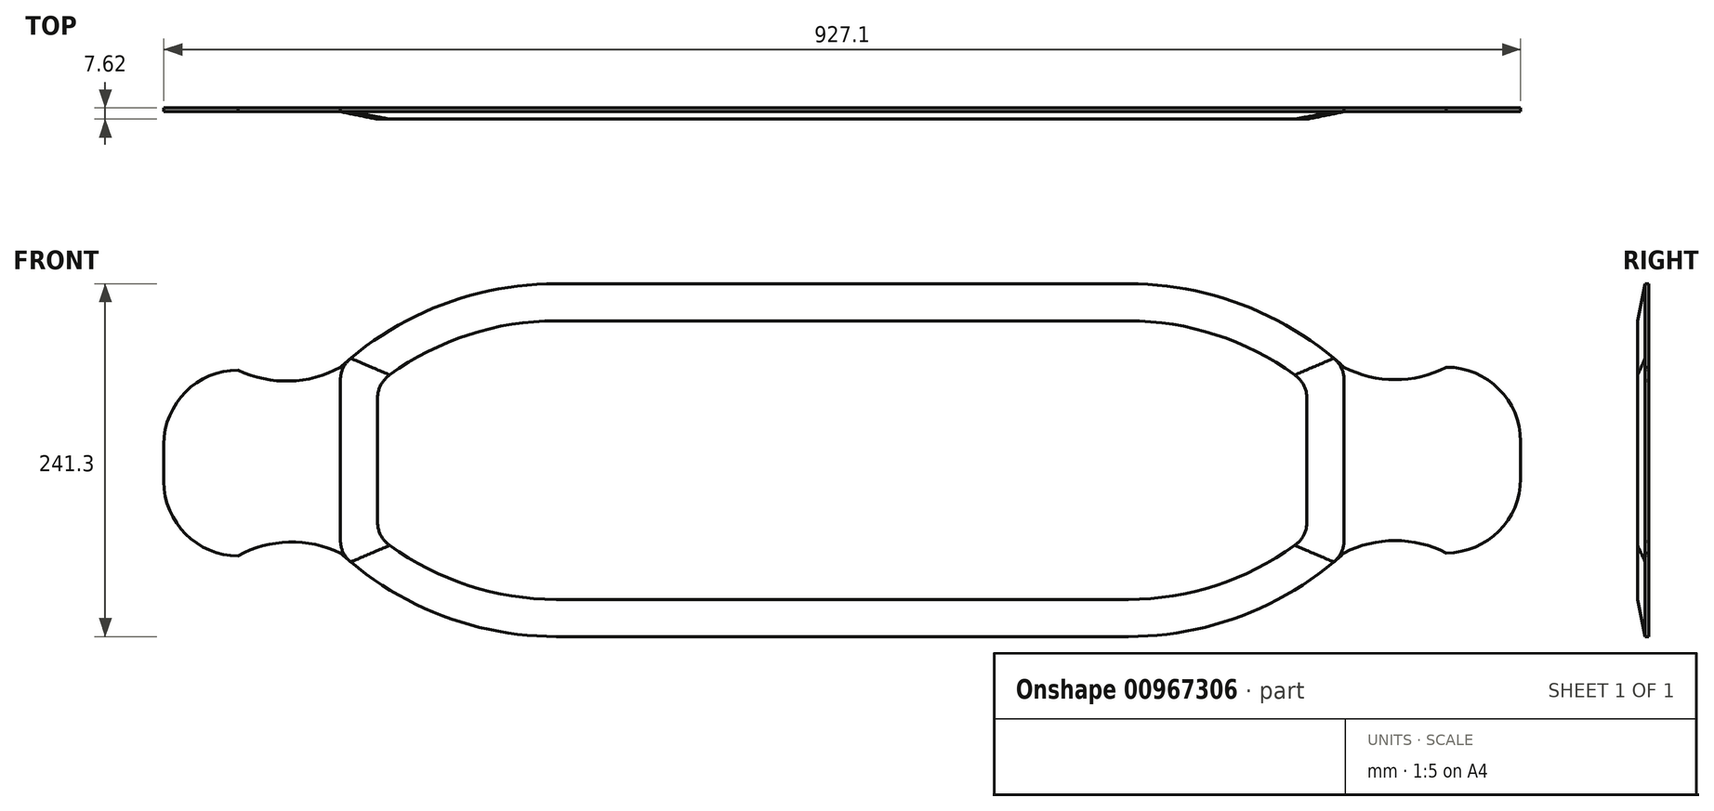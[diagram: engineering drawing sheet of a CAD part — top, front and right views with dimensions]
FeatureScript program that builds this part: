
annotation { "Feature Type Name" : "Feature", "Feature Type Description" : "" }
export const myFeature = defineFeature(function(context is Context, id is Id, definition is map)
    precondition{}
    {
        {
            var Q0;
            Q0=qCreatedBy(makeId("Front.planeOp"),FACE);
            cPlane(context, id + "F0", {"entities" : qUnion([Q0]), "cplaneType" : CPlaneType.OFFSET, "offset" : 6.35 * mm, "width" : 152.4 * mm, "height" : 152.4 * mm});
        }
        {
            var Q0;
            Q0=qCreatedBy(id+"F0.planeOp",FACE);
            var sketch = newSketch(context, id + "F1", { "sketchPlane" : qUnion([Q0])});
            skLineSegment(sketch, "E0.bottom", {"start": v(342.9, -120.65) * mm, "end": v(-342.9, -120.65) * mm});
            skLineSegment(sketch, "E0.top", {"start": v(342.9, 120.65) * mm, "end": v(-342.9, 120.65) * mm});
            skLineSegment(sketch, "E0.left", {"start": v(342.9, -120.65) * mm, "end": v(342.9, 120.65) * mm});
            skLineSegment(sketch, "E0.right", {"start": v(-342.9, -120.65) * mm, "end": v(-342.9, 120.65) * mm});
            skSolve(sketch);
        }
        {
            var Q0;
            Q0=makeQuery(id+"F1.imprint","IMPRINT",FACE,{"disambiguationData":[TD([[makeQuery(id+"F1.imprint","IMPRINT",EDGE,{"derivedFrom":sQuery(id+"F1.wireOp",EDGE,"E0.bottom")}),-1.0]])]});
            var sketch = newSketch(context, id + "F2", { "sketchPlane" : qUnion([Q0])});
            skLineSegment(sketch, "E1.left", {"start": v(-463.55, 10.74) * mm, "end": v(-463.55, -14.66) * mm});
            skPoint(sketch, "E1.middle", {"position": v(-403.23, 0) * mm});
            skLineSegment(sketch, "E2.left", {"start": v(463.55, -12.7) * mm, "end": v(463.55, 12.7) * mm});
            skPoint(sketch, "E2.middle", {"position": v(403.23, 0) * mm});
            skPoint(sketch, "E3.visualSharp", {"position": v(-463.55, 63.5) * mm});
            skArc(sketch, "E3.filletArc", {"start": v(-412.77, 61.54) * mm, "mid": v(-448.68, 46.66) * mm, "end": v(-463.55, 10.74) * mm});
            skPoint(sketch, "E4.visualSharp", {"position": v(-463.55, -63.5) * mm});
            skArc(sketch, "E4.filletArc", {"start": v(-463.55, -14.66) * mm, "mid": v(-448.68, -50.57) * mm, "end": v(-412.77, -65.46) * mm});
            skPoint(sketch, "E5.visualSharp", {"position": v(463.55, -63.5) * mm});
            skArc(sketch, "E5.filletArc", {"start": v(412.75, -63.5) * mm, "mid": v(448.67, -48.62) * mm, "end": v(463.55, -12.7) * mm});
            skPoint(sketch, "E6.visualSharp", {"position": v(463.55, 63.5) * mm});
            skArc(sketch, "E6.filletArc", {"start": v(463.55, 12.7) * mm, "mid": v(448.67, 48.62) * mm, "end": v(412.75, 63.5) * mm});
            skArc(sketch, "E7", {"start": v(-412.77, 61.54) * mm, "mid": v(-377.6, 54.04) * mm, "end": v(-342.9, 63.5) * mm});
            skArc(sketch, "E8", {"start": v(-342.9, -63.5) * mm, "mid": v(-378.07, -56) * mm, "end": v(-412.77, -65.46) * mm});
            skArc(sketch, "E9", {"start": v(342.9, 63.5) * mm, "mid": v(377.83, 55.03) * mm, "end": v(412.75, 63.5) * mm});
            skArc(sketch, "E10", {"start": v(412.75, -63.5) * mm, "mid": v(377.82, -55.03) * mm, "end": v(342.9, -63.5) * mm});
            skArc(sketch, "E11", {"start": v(-195.49, 120.65) * mm, "mid": v(-274.54, 105.86) * mm, "end": v(-342.9, 63.5) * mm});
            skArc(sketch, "E12", {"start": v(-342.9, -63.5) * mm, "mid": v(-274.54, -105.86) * mm, "end": v(-195.49, -120.65) * mm});
            skArc(sketch, "E13", {"start": v(195.49, -120.65) * mm, "mid": v(274.54, -105.86) * mm, "end": v(342.9, -63.5) * mm});
            skArc(sketch, "E14", {"start": v(342.9, 63.5) * mm, "mid": v(274.54, 105.86) * mm, "end": v(195.49, 120.65) * mm});
            skLineSegment(sketch, "E15", {"start": v(-195.49, -120.65) * mm, "end": v(195.49, -120.65) * mm});
            skLineSegment(sketch, "E16", {"start": v(195.49, 120.65) * mm, "end": v(-195.49, 120.65) * mm});
            skLineSegment(sketch, "E17", {"start": v(342.9, -63.5) * mm, "end": v(342.9, 63.5) * mm});
            skLineSegment(sketch, "E18", {"start": v(-342.9, -63.5) * mm, "end": v(-342.9, 63.5) * mm});
            skSolve(sketch);
        }
        {
            var Q0;
            Q0=makeQuery(id+"F2.imprint","IMPRINT",FACE,{"disambiguationData":[TD([[makeQuery(id+"F2.imprint","IMPRINT",EDGE,{"derivedFrom":sQuery(id+"F2.wireOp",EDGE,"E2.left")}),1.0]])]});
            var Q1;
            Q1=makeQuery(id+"F2.imprint","IMPRINT",FACE,{"disambiguationData":[TD([[makeQuery(id+"F2.imprint","IMPRINT",EDGE,{"derivedFrom":sQuery(id+"F2.wireOp",EDGE,"E1.left")}),1.0]])]});
            extrude(context, id + "F3", {"entities" : qUnion([Q0, Q1]), "endBound" : BoundingType.SYMMETRIC, "depth" : 2.54 * mm, "offsetDistance" : 25.4 * mm});
        }
        {
            var Q0;
            {var subQ4=sQuery(id+"F2.wireOp",EDGE,"E11");Q0=makeQuery(id+"F2.imprint","IMPRINT",FACE,{"disambiguationData":[TD([[makeQuery(id+"F2.imprint","IMPRINT",EDGE,{"derivedFrom":subQ4}),1.0]])]});}
            extrude(context, id + "F4", {"entities" : qUnion([Q0]), "endBound" : BoundingType.SYMMETRIC, "depth" : 2.54 * mm, "offsetDistance" : 25.4 * mm});
        }
        {
            var Q0;
            Q0=qCreatedBy(makeId("Front.planeOp"),FACE);
            cPlane(context, id + "F5", {"entities" : qUnion([Q0]), "cplaneType" : CPlaneType.OFFSET, "offset" : 12.7 * mm, "width" : 152.4 * mm, "height" : 152.4 * mm});
        }
        {
            var Q0;
            Q0=qCreatedBy(id+"F5.planeOp",FACE);
            var sketch = newSketch(context, id + "F6", { "sketchPlane" : qUnion([Q0])});
            skArc(sketch, "E19.0", {"start": v(195.49, -95.25) * mm, "mid": v(260.23, -84.08) * mm, "end": v(317.5, -51.87) * mm});
            skLineSegment(sketch, "E19.1", {"start": v(-195.49, -95.25) * mm, "end": v(195.49, -95.25) * mm});
            skLineSegment(sketch, "E19.2", {"start": v(317.5, -51.87) * mm, "end": v(317.5, 51.87) * mm});
            skArc(sketch, "E19.3", {"start": v(-317.5, -51.87) * mm, "mid": v(-260.23, -84.08) * mm, "end": v(-195.49, -95.25) * mm});
            skArc(sketch, "E19.4", {"start": v(317.5, 51.87) * mm, "mid": v(260.23, 84.08) * mm, "end": v(195.49, 95.25) * mm});
            skLineSegment(sketch, "E19.5", {"start": v(195.49, 95.25) * mm, "end": v(-195.49, 95.25) * mm});
            skArc(sketch, "E19.6", {"start": v(-195.49, 95.25) * mm, "mid": v(-260.23, 84.08) * mm, "end": v(-317.5, 51.87) * mm});
            skLineSegment(sketch, "E19.7", {"start": v(-317.5, -51.87) * mm, "end": v(-317.5, 51.87) * mm});
            skSolve(sketch);
        }
        {
            var Q1;
            Q1=makeQuery(id+"F6.imprint","IMPRINT",FACE,{"disambiguationData":[TD([[makeQuery(id+"F6.imprint","IMPRINT",EDGE,{"derivedFrom":sQuery(id+"F6.wireOp",EDGE,"E19.0")}),1.0]])]});
            var Q2;
            Q2=makeQuery(id+"F4.opExtrude","CAP_FACE",FACE,{"disambiguationData":[OSD([sQuery(id+"F2.wireOp",EDGE,"E11"),sQuery(id+"F2.wireOp",EDGE,"E12"),sQuery(id+"F2.wireOp",EDGE,"E13"),sQuery(id+"F2.wireOp",EDGE,"E14"),sQuery(id+"F2.wireOp",EDGE,"E15"),sQuery(id+"F2.wireOp",EDGE,"E16"),sQuery(id+"F2.wireOp",EDGE,"E17"),sQuery(id+"F2.wireOp",EDGE,"E18")])],"isStart":false});
            loft(context, id + "F7", {"operationType" : NewBodyOperationType.ADD, "sheetProfilesArray" : [{ "sheetProfileEntities" : qUnion([Q1]) }, { "sheetProfileEntities" : qUnion([Q2]) }]});
        }
        {
            var Q0;
            Q0=makeQuery(id+"F7.opLoft","SWEPT_EDGE",EDGE,{"disambiguationData":[OSD([sQuery(id+"F1.wireOp",EDGE,"E0.right"),sQuery(id+"F2.wireOp",EDGE,"E7"),sQuery(id+"F2.wireOp",EDGE,"E11"),sQuery(id+"F2.wireOp",EDGE,"E18"),sQuery(id+"F6.wireOp",EDGE,"E19.6"),sQuery(id+"F6.wireOp",EDGE,"E19.7")])]});
            var Q1;
            Q1=makeQuery(id+"F7.opLoft","SWEPT_EDGE",EDGE,{"disambiguationData":[OSD([sQuery(id+"F1.wireOp",EDGE,"E0.right"),sQuery(id+"F2.wireOp",EDGE,"E8"),sQuery(id+"F2.wireOp",EDGE,"E12"),sQuery(id+"F2.wireOp",EDGE,"E18"),sQuery(id+"F6.wireOp",EDGE,"E19.3"),sQuery(id+"F6.wireOp",EDGE,"E19.7")])]});
            fillet(context, id + "F8", {"entities" : qUnion([Q0, Q1]), "radius" : 101.6 * mm, "tangentPropagation" : true, "allowEdgeOverflow" : false});
        }
        {
            var Q0;
            Q0=makeQuery(id+"F7.opLoft","SWEPT_EDGE",EDGE,{"disambiguationData":[OSD([sQuery(id+"F1.wireOp",EDGE,"E0.left"),sQuery(id+"F2.wireOp",EDGE,"E10"),sQuery(id+"F2.wireOp",EDGE,"E13"),sQuery(id+"F2.wireOp",EDGE,"E17"),sQuery(id+"F6.wireOp",EDGE,"E19.0"),sQuery(id+"F6.wireOp",EDGE,"E19.2")])]});
            var Q1;
            Q1=makeQuery(id+"F7.opLoft","SWEPT_EDGE",EDGE,{"disambiguationData":[OSD([sQuery(id+"F1.wireOp",EDGE,"E0.left"),sQuery(id+"F2.wireOp",EDGE,"E9"),sQuery(id+"F2.wireOp",EDGE,"E14"),sQuery(id+"F2.wireOp",EDGE,"E17"),sQuery(id+"F6.wireOp",EDGE,"E19.2"),sQuery(id+"F6.wireOp",EDGE,"E19.4")])]});
            fillet(context, id + "F9", {"entities" : qUnion([Q0, Q1]), "radius" : 101.6 * mm, "tangentPropagation" : true, "allowEdgeOverflow" : false});
        }
    });
